# Revit family: 6088IN-0 Family
name_source: partatom
category: Plumbing Fixtures
revit_build: Autodesk Revit 2018 (Build: 20180329_1100(x64)
units: mm (PartAtom-declared; Revit-internal decimal feet)

## family parameters
Always vertical = Yes
Cut with Voids When Loaded = No
Host = Wall
OmniClass Number = 23.45.00.00
OmniClass Title = Sanitary, Laundry, and Cleaning Equipment
Part Type = Normal
Room Calculation Point = No
Round Connector Dimension = Use Diameter
Shared = No

## types (1)
- 6088IN-0
    Description = Replay Wall Hung Bowl Only
    Distance from floor = 500 mm  [stored 1.64042 ft]
    Height = 391 mm
    Length = 591 mm
    Manufacturer = Kohler
    Material = Vitreous China
    Model = 6088IN-0 Replay Wall Hung Bowl
    URL = www.us.kohler.com
    Width = 434 mm  [stored 1.42388 ft]

note: [stored X ft] marks values corroborated as IEEE doubles in the binary element streams (Revit-internal decimal feet)

## geometry (parser evidence)
native form markers: Sweep x3
no freeform markers — native parametric forms only
